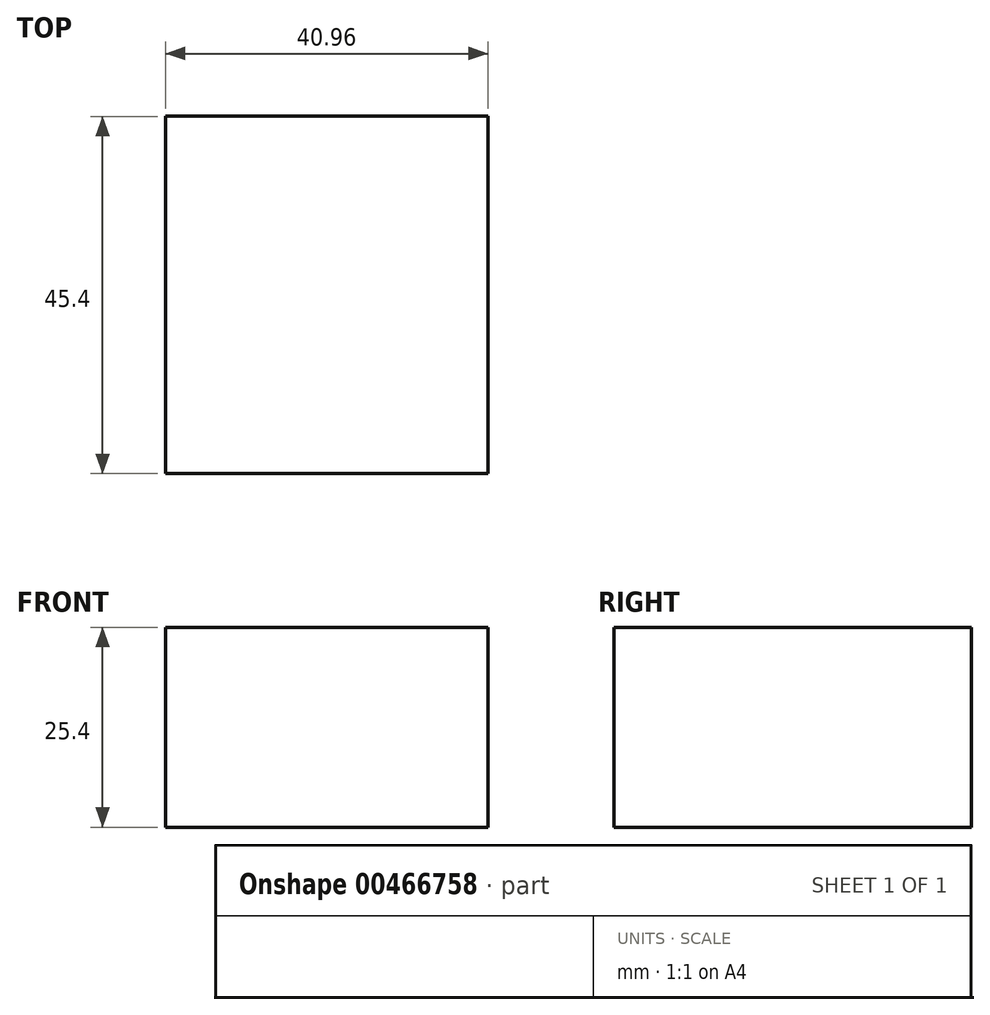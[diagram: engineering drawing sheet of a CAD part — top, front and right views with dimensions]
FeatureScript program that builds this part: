
annotation { "Feature Type Name" : "Feature", "Feature Type Description" : "" }
export const myFeature = defineFeature(function(context is Context, id is Id, definition is map)
    precondition{}
    {
        {
            var Q0;
            Q0=qCreatedBy(makeId("Top.planeOp"),FACE);
            var sketch = newSketch(context, id + "F0", { "sketchPlane" : qUnion([Q0])});
            skLineSegment(sketch, "E0.bottom", {"start": v(-29.18, 0) * mm, "end": v(-35.42, 0) * mm});
            skLineSegment(sketch, "E0.top", {"start": v(-29.18, 23.87) * mm, "end": v(-35.42, 23.87) * mm});
            skLineSegment(sketch, "E0.left", {"start": v(-29.18, 0) * mm, "end": v(-29.18, 23.87) * mm});
            skLineSegment(sketch, "E0.right", {"start": v(-35.42, 0) * mm, "end": v(-35.42, 23.87) * mm});
            skLineSegment(sketch, "E1.bottom", {"start": v(10.8, 0) * mm, "end": v(51.75, 0) * mm});
            skLineSegment(sketch, "E1.top", {"start": v(10.8, 45.4) * mm, "end": v(51.75, 45.4) * mm});
            skLineSegment(sketch, "E1.left", {"start": v(10.8, 0) * mm, "end": v(10.8, 45.4) * mm});
            skLineSegment(sketch, "E1.right", {"start": v(51.75, 0) * mm, "end": v(51.75, 45.4) * mm});
            skSolve(sketch);
        }
        {
            var Q0;
            Q0=makeQuery(id+"F0.imprint","IMPRINT",FACE,{"disambiguationData":[TD([[makeQuery(id+"F0.imprint","IMPRINT",EDGE,{"derivedFrom":sQuery(id+"F0.wireOp",EDGE,"E1.bottom")}),1.0]])]});
            extrude(context, id + "F1", {"entities" : qUnion([Q0]), "depth" : 25.4 * mm});
        }
    });
